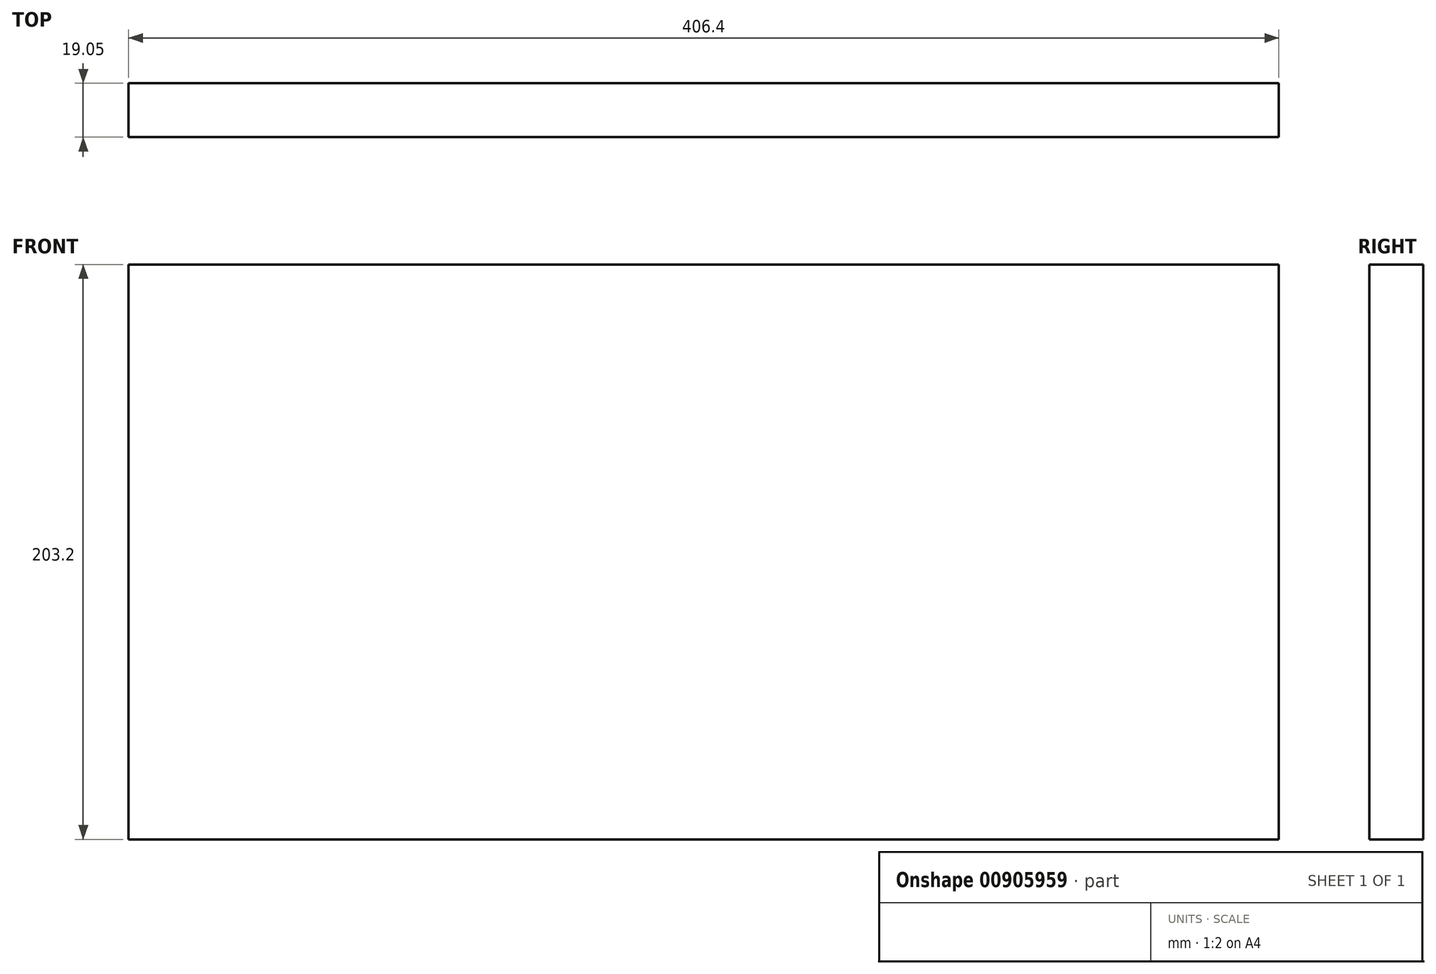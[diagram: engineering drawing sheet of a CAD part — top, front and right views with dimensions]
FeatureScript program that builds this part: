
annotation { "Feature Type Name" : "Feature", "Feature Type Description" : "" }
export const myFeature = defineFeature(function(context is Context, id is Id, definition is map)
    precondition{}
    {
        {
            var Q0;
            Q0=qCreatedBy(makeId("Front.planeOp"),FACE);
            var sketch = newSketch(context, id + "F0", { "sketchPlane" : qUnion([Q0])});
            skLineSegment(sketch, "E0.bottom", {"start": v(0, 0) * mm, "end": v(406.4, 0) * mm});
            skLineSegment(sketch, "E0.top", {"start": v(0, 203.2) * mm, "end": v(406.4, 203.2) * mm});
            skLineSegment(sketch, "E0.left", {"start": v(0, 0) * mm, "end": v(0, 203.2) * mm});
            skLineSegment(sketch, "E0.right", {"start": v(406.4, 0) * mm, "end": v(406.4, 203.2) * mm});
            skSolve(sketch);
        }
        {
            var Q0;
            Q0 = qSketchRegion(id + "F0", true);
            extrude(context, id + "F1", {"entities" : qUnion([Q0]), "depth" : 19.05 * mm, "offsetDistance" : 25.4 * mm});
        }
    });
